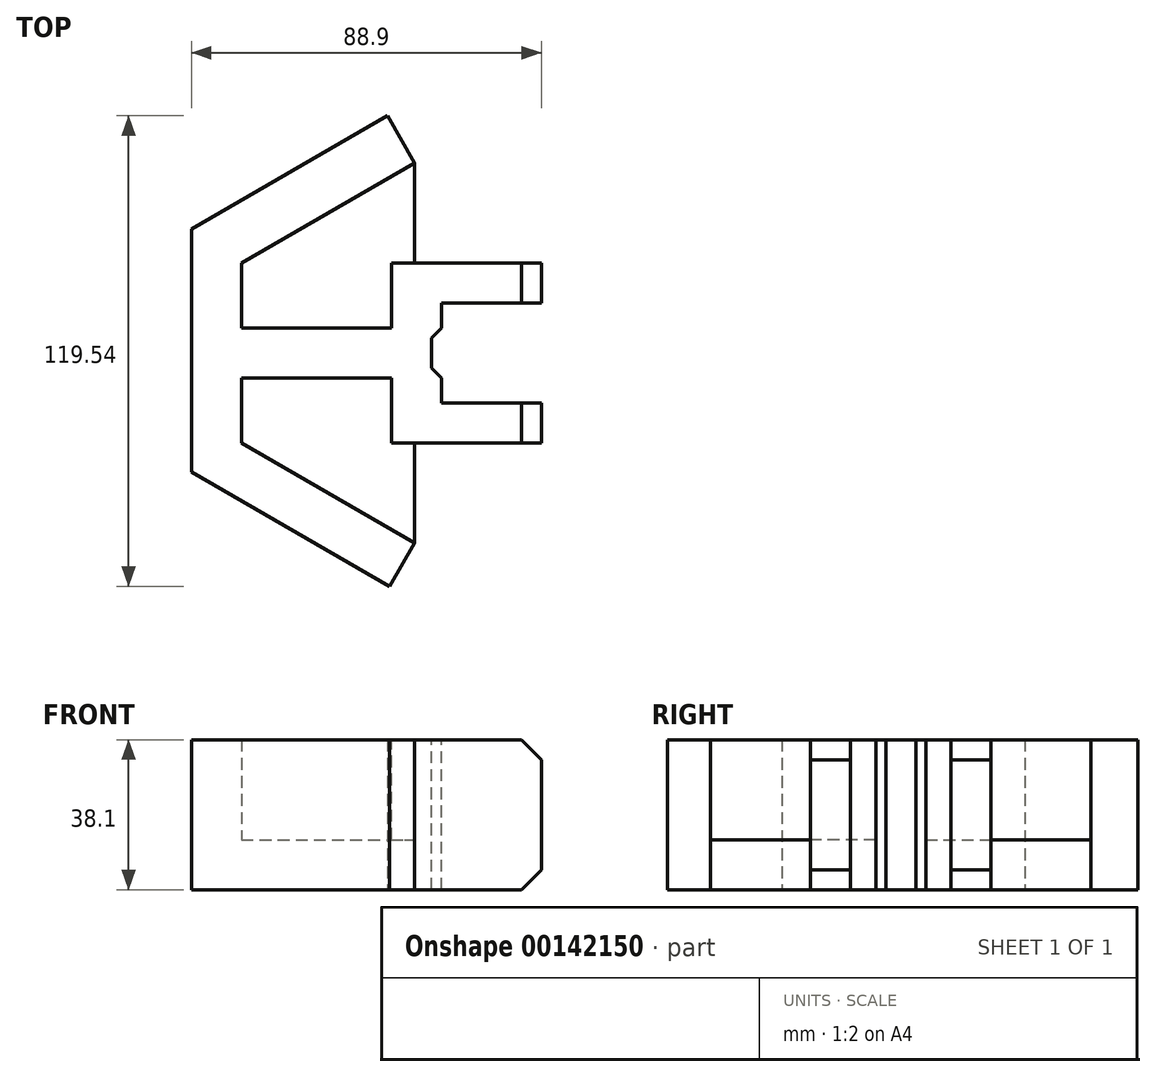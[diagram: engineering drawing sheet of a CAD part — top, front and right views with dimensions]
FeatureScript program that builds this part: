
annotation { "Feature Type Name" : "Feature", "Feature Type Description" : "" }
export const myFeature = defineFeature(function(context is Context, id is Id, definition is map)
    precondition{}
    {
        {
            var Q0;
            Q0=qCreatedBy(makeId("Top.planeOp"),FACE);
            var sketch = newSketch(context, id + "F0", { "sketchPlane" : qUnion([Q0])});
            skLineSegment(sketch, "E0", {"start": v(0, 25.43) * mm, "end": v(0, 0) * mm});
            skLineSegment(sketch, "E1", {"start": v(0, 0) * mm, "end": v(25.4, 0) * mm});
            skLineSegment(sketch, "E2", {"start": v(0, 25.43) * mm, "end": v(25.4, 25.43) * mm});
            skLineSegment(sketch, "E3", {"start": v(25.4, 25.43) * mm, "end": v(25.4, 35.59) * mm});
            skLineSegment(sketch, "E4", {"start": v(25.4, 35.59) * mm, "end": v(-50.8, 35.59) * mm});
            skLineSegment(sketch, "E5", {"start": v(25.4, 0) * mm, "end": v(25.4, -10.16) * mm});
            skLineSegment(sketch, "E6", {"start": v(25.4, -10.16) * mm, "end": v(-50.8, -10.16) * mm});
            skLineSegment(sketch, "E7", {"start": v(-50.8, -10.16) * mm, "end": v(-50.8, 35.59) * mm});
            skSolve(sketch);
        }
        {
            var Q0;
            Q0=makeQuery(id+"F0.imprint","IMPRINT",FACE,{"disambiguationData":[TD([[makeQuery(id+"F0.imprint","IMPRINT",EDGE,{"derivedFrom":sQuery(id+"F0.wireOp",EDGE,"E0")}),-1.0]])]});
            extrude(context, id + "F1", {"entities" : qUnion([Q0]), "depth" : 38.1 * mm});
        }
        {
            var Q0;
            Q0=makeQuery(id+"F1.opExtrude","CAP_EDGE",EDGE,{"disambiguationData":[OSD([sQuery(id+"F0.wireOp",EDGE,"E5")])],"isStart":true});
            var Q1;
            Q1=makeQuery(id+"F1.opExtrude","CAP_EDGE",EDGE,{"disambiguationData":[OSD([sQuery(id+"F0.wireOp",EDGE,"E3")])],"isStart":true});
            var Q2;
            Q2=makeQuery(id+"F1.opExtrude","CAP_EDGE",EDGE,{"disambiguationData":[OSD([sQuery(id+"F0.wireOp",EDGE,"E5")])],"isStart":false});
            var Q3;
            Q3=makeQuery(id+"F1.opExtrude","CAP_EDGE",EDGE,{"disambiguationData":[OSD([sQuery(id+"F0.wireOp",EDGE,"E3")])],"isStart":false});
            chamfer(context, id + "F2", {"entities" : qUnion([Q0, Q1, Q2, Q3]), "width" : 5.08 * mm, "tangentPropagation" : true});
        }
        {
            var Q0;
            Q0=makeQuery(id+"F1.opExtrude","CAP_FACE",FACE,{"disambiguationData":[OSD([sQuery(id+"F0.wireOp",EDGE,"E0"),sQuery(id+"F0.wireOp",EDGE,"E1"),sQuery(id+"F0.wireOp",EDGE,"E2"),sQuery(id+"F0.wireOp",EDGE,"E3"),sQuery(id+"F0.wireOp",EDGE,"E4"),sQuery(id+"F0.wireOp",EDGE,"E5"),sQuery(id+"F0.wireOp",EDGE,"E6"),sQuery(id+"F0.wireOp",EDGE,"E7")])],"isStart":true});
            var sketch = newSketch(context, id + "F3", { "sketchPlane" : qUnion([Q0])});
            skLineSegment(sketch, "E8", {"start": v(-50.8, 10.16) * mm, "end": v(-6.8, 35.56) * mm});
            skLineSegment(sketch, "E9", {"start": v(-50.8, -35.59) * mm, "end": v(-6.8, -60.99) * mm});
            skLineSegment(sketch, "E10", {"start": v(-6.8, -60.99) * mm, "end": v(-13.73, -72.98) * mm});
            skLineSegment(sketch, "E11", {"start": v(-50.8, -35.59) * mm, "end": v(-50.8, 10.16) * mm});
            skLineSegment(sketch, "E12", {"start": v(-63.5, -35.59) * mm, "end": v(-63.5, 10.16) * mm});
            skLineSegment(sketch, "E13", {"start": v(-13.73, -72.98) * mm, "end": v(-63.5, -44.25) * mm});
            skLineSegment(sketch, "E14", {"start": v(-63.5, -44.25) * mm, "end": v(-63.5, -35.59) * mm});
            skLineSegment(sketch, "E15", {"start": v(-6.8, 35.56) * mm, "end": v(-13.16, 46.56) * mm});
            skLineSegment(sketch, "E16", {"start": v(-13.16, 46.56) * mm, "end": v(-63.5, 17.5) * mm});
            skLineSegment(sketch, "E17", {"start": v(-63.5, 17.5) * mm, "end": v(-63.5, 10.16) * mm});
            skSolve(sketch);
        }
        {
            var Q0;
            Q0=makeQuery(id+"F3.imprint","IMPRINT",FACE,{"disambiguationData":[TD([[makeQuery(id+"F3.imprint","IMPRINT",EDGE,{"derivedFrom":sQuery(id+"F3.wireOp",EDGE,"E8")}),1.0]])]});
            extrude(context, id + "F4", {"entities" : qUnion([Q0]), "operationType" : NewBodyOperationType.ADD, "oppositeDirection" : true, "depth" : 38.1 * mm});
        }
        {
            var Q0;
            Q0=makeQuery(id+"F4.boolean.opBoolean","MERGE",FACE,{"derivedFrom":[makeQuery(id+"F1.opExtrude","CAP_FACE",FACE,{"disambiguationData":[OSD([sQuery(id+"F0.wireOp",EDGE,"E0"),sQuery(id+"F0.wireOp",EDGE,"E1"),sQuery(id+"F0.wireOp",EDGE,"E2"),sQuery(id+"F0.wireOp",EDGE,"E3"),sQuery(id+"F0.wireOp",EDGE,"E4"),sQuery(id+"F0.wireOp",EDGE,"E5"),sQuery(id+"F0.wireOp",EDGE,"E6"),sQuery(id+"F0.wireOp",EDGE,"E7")])],"isStart":true}),makeQuery(id+"F4.opExtrude","CAP_FACE",FACE,{"disambiguationData":[OSD([sQuery(id+"F3.wireOp",EDGE,"E8"),sQuery(id+"F3.wireOp",EDGE,"E9"),sQuery(id+"F3.wireOp",EDGE,"E10"),sQuery(id+"F3.wireOp",EDGE,"E11"),sQuery(id+"F3.wireOp",EDGE,"E12"),sQuery(id+"F3.wireOp",EDGE,"E13"),sQuery(id+"F3.wireOp",EDGE,"E14"),sQuery(id+"F3.wireOp",EDGE,"E15"),sQuery(id+"F3.wireOp",EDGE,"E16"),sQuery(id+"F3.wireOp",EDGE,"E17")])],"isStart":true})]});
            var sketch = newSketch(context, id + "F5", { "sketchPlane" : qUnion([Q0])});
            skLineSegment(sketch, "E18", {"start": v(-6.8, 35.56) * mm, "end": v(-6.8, -60.99) * mm});
            skLineSegment(sketch, "E19", {"start": v(-6.8, -60.99) * mm, "end": v(-50.8, -35.59) * mm});
            skLineSegment(sketch, "E20", {"start": v(-50.8, -35.59) * mm, "end": v(-50.8, 10.16) * mm});
            skLineSegment(sketch, "E21", {"start": v(-50.8, 10.16) * mm, "end": v(-6.8, 35.56) * mm});
            skSolve(sketch);
        }
        {
            var Q0;
            Q0 = qSketchRegion(id + "F5", true);
            extrude(context, id + "F6", {"entities" : qUnion([Q0]), "operationType" : NewBodyOperationType.ADD, "oppositeDirection" : true, "depth" : 12.7 * mm});
        }
        {
            var Q0;
            Q0=makeQuery(id+"F4.boolean.opBoolean","MERGE",FACE,{"derivedFrom":[makeQuery(id+"F1.opExtrude","CAP_FACE",FACE,{"disambiguationData":[OSD([sQuery(id+"F0.wireOp",EDGE,"E0"),sQuery(id+"F0.wireOp",EDGE,"E1"),sQuery(id+"F0.wireOp",EDGE,"E2"),sQuery(id+"F0.wireOp",EDGE,"E3"),sQuery(id+"F0.wireOp",EDGE,"E4"),sQuery(id+"F0.wireOp",EDGE,"E5"),sQuery(id+"F0.wireOp",EDGE,"E6"),sQuery(id+"F0.wireOp",EDGE,"E7")])],"isStart":false}),makeQuery(id+"F4.opExtrude","CAP_FACE",FACE,{"disambiguationData":[OSD([sQuery(id+"F3.wireOp",EDGE,"E8"),sQuery(id+"F3.wireOp",EDGE,"E9"),sQuery(id+"F3.wireOp",EDGE,"E10"),sQuery(id+"F3.wireOp",EDGE,"E11"),sQuery(id+"F3.wireOp",EDGE,"E12"),sQuery(id+"F3.wireOp",EDGE,"E13"),sQuery(id+"F3.wireOp",EDGE,"E14"),sQuery(id+"F3.wireOp",EDGE,"E15"),sQuery(id+"F3.wireOp",EDGE,"E16"),sQuery(id+"F3.wireOp",EDGE,"E17")])],"isStart":false})]});
            var sketch = newSketch(context, id + "F7", { "sketchPlane" : qUnion([Q0])});
            skLineSegment(sketch, "E22", {"start": v(-50.8, -10.16) * mm, "end": v(-50.8, 6.36) * mm});
            skLineSegment(sketch, "E23", {"start": v(-50.8, 6.36) * mm, "end": v(-12.7, 6.36) * mm});
            skLineSegment(sketch, "E24", {"start": v(-12.7, 6.36) * mm, "end": v(-12.7, -10.16) * mm});
            skLineSegment(sketch, "E25", {"start": v(-50.8, 19.03) * mm, "end": v(-12.7, 19.03) * mm});
            skLineSegment(sketch, "E26", {"start": v(-12.7, 19.03) * mm, "end": v(-12.7, 35.59) * mm});
            skLineSegment(sketch, "E27", {"start": v(-12.7, 35.59) * mm, "end": v(-50.8, 35.59) * mm});
            skLineSegment(sketch, "E28", {"start": v(-12.7, -10.16) * mm, "end": v(-50.8, -10.16) * mm});
            skLineSegment(sketch, "E29.trimOffspring", {"start": v(-50.8, 19.03) * mm, "end": v(-50.8, 35.59) * mm});
            skPoint(sketch, "E30.orphan", {"position": v(-50.8, 12.71) * mm});
            skSolve(sketch);
        }
        {
            var Q0;
            Q0=makeQuery(id+"F7.imprint","IMPRINT",FACE,{"disambiguationData":[TD([[makeQuery(id+"F7.imprint","IMPRINT",EDGE,{"derivedFrom":sQuery(id+"F7.wireOp",EDGE,"E22")}),-1.0]])]});
            var Q1;
            Q1=makeQuery(id+"F7.imprint","IMPRINT",FACE,{"disambiguationData":[TD([[makeQuery(id+"F7.imprint","IMPRINT",EDGE,{"derivedFrom":sQuery(id+"F7.wireOp",EDGE,"E25")}),1.0]])]});
            var Q2;
            {var subQ0=sQuery(id+"F5.wireOp",EDGE,"E18");Q2=makeQuery(id+"F6.boolean.opBoolean","SPLIT",FACE,{"disambiguationData":[TD([makeQuery(id+"F1.opExtrude","SWEPT_FACE",FACE,{"disambiguationData":[OSD([sQuery(id+"F0.wireOp",EDGE,"E6")])]})])],"derivedFrom":makeQuery(id+"F6.opExtrude","CAP_FACE",FACE,{"disambiguationData":[OSD([subQ0,sQuery(id+"F5.wireOp",EDGE,"E19"),sQuery(id+"F5.wireOp",EDGE,"E20"),sQuery(id+"F5.wireOp",EDGE,"E21")])],"isStart":false})});}
            extrude(context, id + "F8", {"entities" : qUnion([Q0, Q1]), "operationType" : NewBodyOperationType.REMOVE, "endBound" : BoundingType.UP_TO_SURFACE, "oppositeDirection" : true, "endBoundEntityFace" : qUnion([Q2]), "depth" : 25.4 * mm});
        }
        {
            var Q0;
            Q0=makeQuery(id+"F4.boolean.opBoolean","MERGE",FACE,{"derivedFrom":[makeQuery(id+"F1.opExtrude","CAP_FACE",FACE,{"disambiguationData":[OSD([sQuery(id+"F0.wireOp",EDGE,"E0"),sQuery(id+"F0.wireOp",EDGE,"E1"),sQuery(id+"F0.wireOp",EDGE,"E2"),sQuery(id+"F0.wireOp",EDGE,"E3"),sQuery(id+"F0.wireOp",EDGE,"E4"),sQuery(id+"F0.wireOp",EDGE,"E5"),sQuery(id+"F0.wireOp",EDGE,"E6"),sQuery(id+"F0.wireOp",EDGE,"E7")])],"isStart":false}),makeQuery(id+"F4.opExtrude","CAP_FACE",FACE,{"disambiguationData":[OSD([sQuery(id+"F3.wireOp",EDGE,"E8"),sQuery(id+"F3.wireOp",EDGE,"E9"),sQuery(id+"F3.wireOp",EDGE,"E10"),sQuery(id+"F3.wireOp",EDGE,"E11"),sQuery(id+"F3.wireOp",EDGE,"E12"),sQuery(id+"F3.wireOp",EDGE,"E13"),sQuery(id+"F3.wireOp",EDGE,"E14"),sQuery(id+"F3.wireOp",EDGE,"E15"),sQuery(id+"F3.wireOp",EDGE,"E16"),sQuery(id+"F3.wireOp",EDGE,"E17")])],"isStart":false})]});
            var sketch = newSketch(context, id + "F9", { "sketchPlane" : qUnion([Q0])});
            skPoint(sketch, "E31.endSnap0", {"position": v(0, 12.71) * mm});
            skLineSegment(sketch, "E32", {"start": v(-2.54, 8.9) * mm, "end": v(0, 6.36) * mm});
            skLineSegment(sketch, "E33", {"start": v(0, 19.06) * mm, "end": v(-2.54, 16.52) * mm});
            skPoint(sketch, "E34.start.orphan", {"position": v(-2.54, 12.71) * mm});
            skLineSegment(sketch, "E35", {"start": v(-2.54, 8.9) * mm, "end": v(-2.54, 16.52) * mm});
            skLineSegment(sketch, "E36", {"start": v(0, 19.06) * mm, "end": v(0, 6.36) * mm});
            skSolve(sketch);
        }
        {
            var Q0;
            Q0=makeQuery(id+"F9.imprint","IMPRINT",FACE,{"disambiguationData":[TD([[makeQuery(id+"F9.imprint","IMPRINT",EDGE,{"derivedFrom":sQuery(id+"F9.wireOp",EDGE,"E32")}),1.0]])]});
            extrude(context, id + "F10", {"entities" : qUnion([Q0]), "operationType" : NewBodyOperationType.REMOVE, "endBound" : BoundingType.THROUGH_ALL, "oppositeDirection" : true, "depth" : 25.4 * mm});
        }
    });
